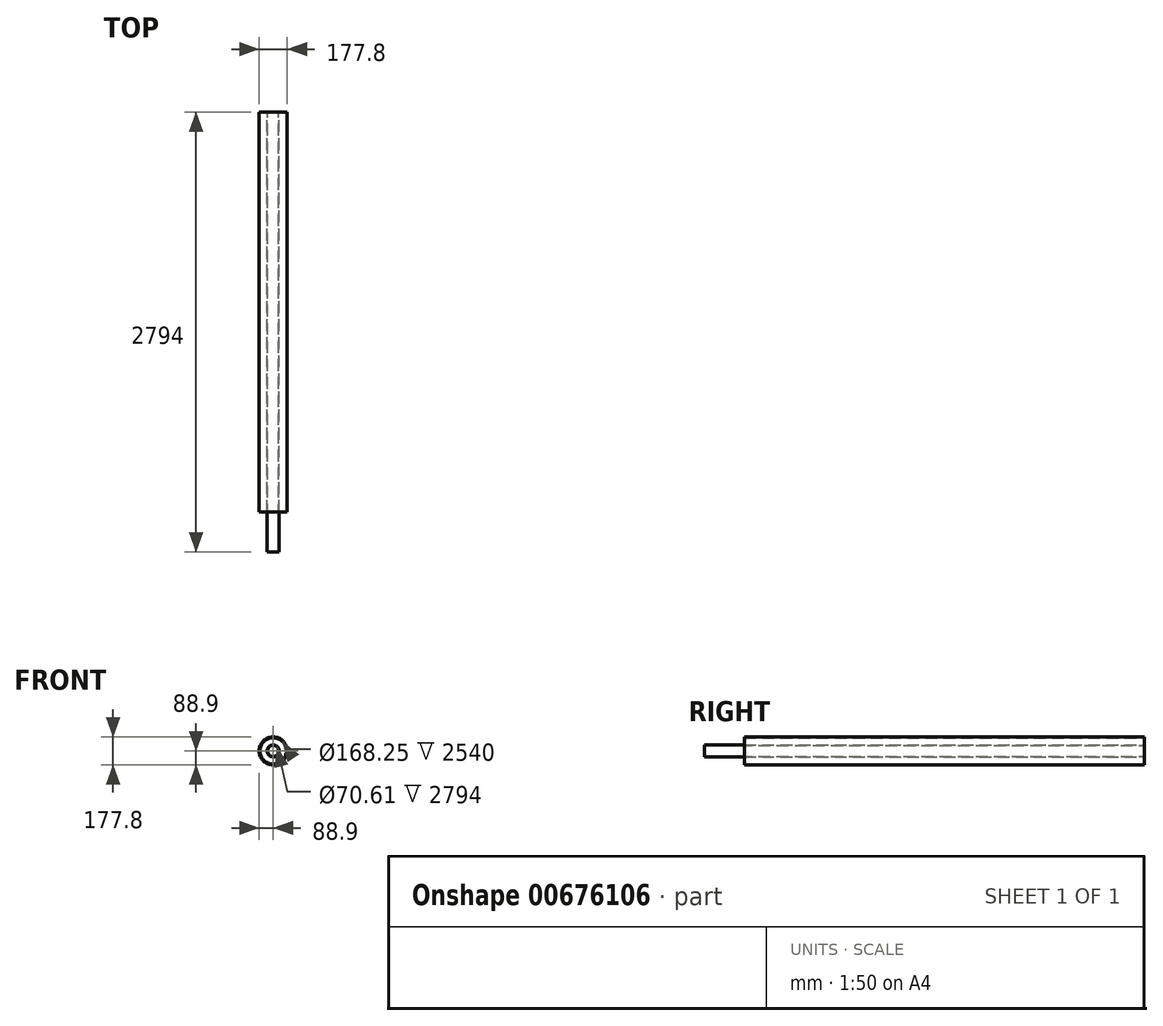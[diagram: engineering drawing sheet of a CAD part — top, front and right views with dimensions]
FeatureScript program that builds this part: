
annotation { "Feature Type Name" : "Feature", "Feature Type Description" : "" }
export const myFeature = defineFeature(function(context is Context, id is Id, definition is map)
    precondition{}
    {
        {
            var Q0;
            Q0=qCreatedBy(makeId("Front.planeOp"),FACE);
            var sketch = newSketch(context, id + "F0", { "sketchPlane" : qUnion([Q0])});
            skCircle(sketch, "E0", {"center": v(0, 0) * mm, "radius": 88.9 * mm});
            skCircle(sketch, "E1", {"center": v(0, 0) * mm, "radius": 38.1 * mm});
            skCircle(sketch, "E2", {"center": v(0, 0) * mm, "radius": 35.3 * mm});
            skCircle(sketch, "E3", {"center": v(0, 0) * mm, "radius": 84.13 * mm});
            skSolve(sketch);
        }
        {
            var Q0;
            Q0 = qSketchRegion(id + "F0", true);
            var Q1;
            Q1=makeQuery(id+"F0.imprint","IMPRINT",FACE,{"disambiguationData":[TD([[makeQuery(id+"F0.imprint","IMPRINT",EDGE,{"derivedFrom":sQuery(id+"F0.wireOp",EDGE,"E1")}),1.0]])]});
            extrude(context, id + "F1", {"entities" : qUnion([Q0, Q1]), "depth" : 2540 * mm, "offsetDistance" : 25.4 * mm});
        }
        {
            var Q0;
            Q0=sQuery(id+"F0.wireOp",EDGE,"E0");
            extrude(context, id + "F2", {"bodyType" : ToolBodyType.SURFACE, "surfaceEntities" : qUnion([Q0]), "depth" : -254 * mm, "offsetDistance" : 25.4 * mm});
        }
        {
            var Q0;
            Q0=makeQuery(id+"F1.opExtrude","CAP_FACE",FACE,{"disambiguationData":[OSD([sQuery(id+"F0.wireOp",EDGE,"E1"),sQuery(id+"F0.wireOp",EDGE,"E2")])],"isStart":false});
            extrude(context, id + "F3", {"entities" : qUnion([Q0]), "operationType" : NewBodyOperationType.ADD, "depth" : 254 * mm, "offsetDistance" : 25.4 * mm});
        }
    });
